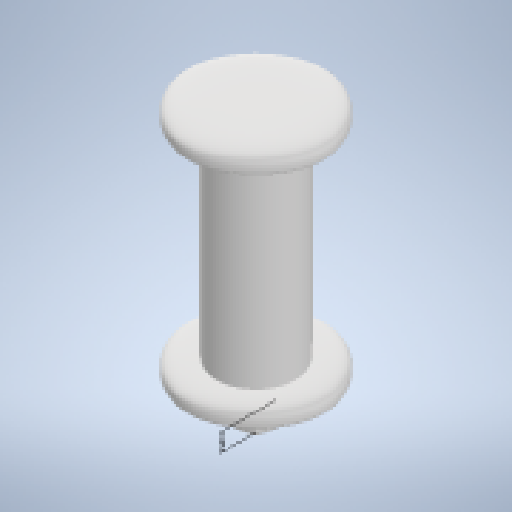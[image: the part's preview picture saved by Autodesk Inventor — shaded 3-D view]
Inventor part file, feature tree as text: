
AUTODESK INVENTOR PART (.ipt)
format: ipt  version: 2025 (Build 290162010, 162A)  size: 544,768 bytes
history: native  units: mm
features: sketch x5, extrude x4, other x2, hole x2, fillet x1, chamfer x1
ambient origin geometry x8: Origin, YZ Plane, XZ Plane, XY Plane, X Axis, Y Axis, Z Axis, Center Point
bodies: Volumenkörper5 (feature_tree), Volumenkörper6 (feature_tree), Volumenkörper8 (feature_tree)
feature tree (15):
  extrude  "Extrusion4"  Depth=100.0mm TaperAngle=0.0deg
  other  "Form5"
  other  "Form7"
  extrude  "Extrusion5"  Depth=20.0mm
  extrude  "Extrusion7"  Depth=204.0mm TaperAngle=0.0deg
  extrude  "Extrusion6"  Depth=4.0mm
  fillet  "Rundung2"  Radius=9.0mm
  sketch  "Skizze10"  dims[d50=2.459mm d51=6.0mm d52=6.3mm d53=2.0mm d54=90.0deg d55=5.0mm d56=20.594885mm d57=3.2mm d58=9.0mm d59=6.3mm d60=2.0mm d61=90.0deg d62=8.0mm d63=20.594885mm d64=2.0mm d65=2.0mm d66=45.0deg]
  hole  "Bohrung3"  [1 undecoded]
  hole  "Bohrung4"  [1 undecoded]
  chamfer  "Fasen2"  [1 undecoded]
  sketch  "Skizze6"  dims[d35=40.0mm d36=100.0mm d37=0.0mm]
  sketch  "Skizze7"  dims[d38=5.0mm d39=105.0mm d40=0.0mm d41=0.0mm d42=20.0mm]
  sketch  "Skizze8"  dims[d43=20.0mm d44=204.0mm d45=0.0mm]
  sketch  "Skizze9"  dims[d46=18.0mm d47=0.0mm d48=4.0mm d49=9.0mm]
note: 3 required parameter values undecoded (feature->parameter linkage not recoverable at this tier; creation-order binding heuristic only, values carry confidence <= 0.55)
